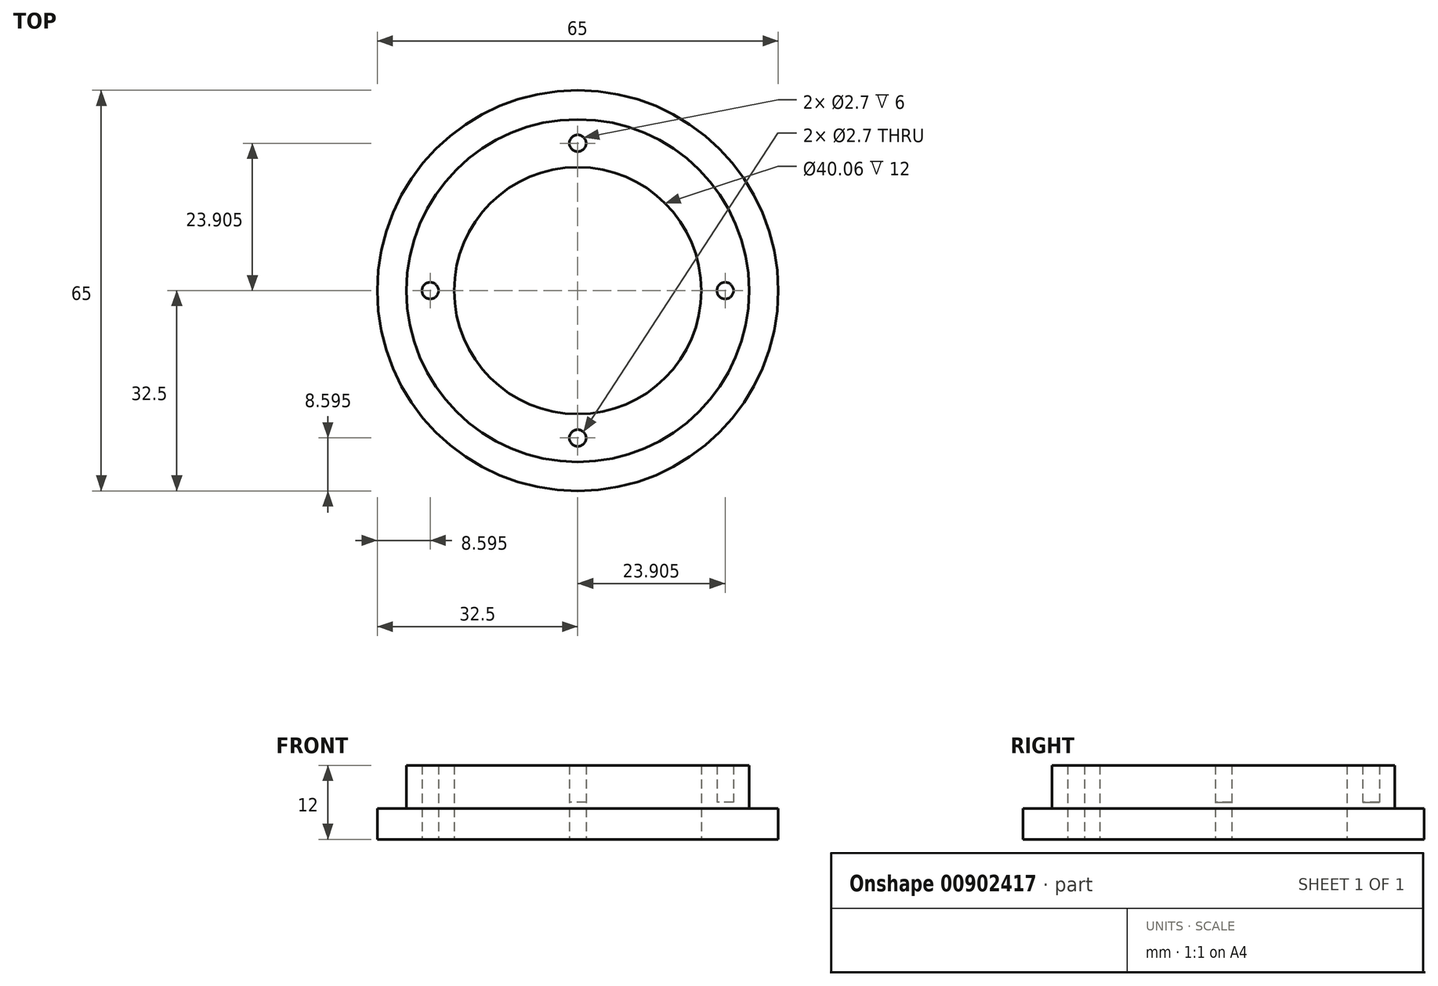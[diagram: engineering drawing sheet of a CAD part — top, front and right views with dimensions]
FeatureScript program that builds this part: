
annotation { "Feature Type Name" : "Feature", "Feature Type Description" : "" }
export const myFeature = defineFeature(function(context is Context, id is Id, definition is map)
    precondition{}
    {
        {
            var Q0;
            Q0=qCreatedBy(makeId("Top.planeOp"),FACE);
            var sketch = newSketch(context, id + "F0", { "sketchPlane" : qUnion([Q0])});
            skCircle(sketch, "E0", {"center": v(0, 0) * mm, "radius": 32.5 * mm});
            skCircle(sketch, "E1.0", {"center": v(0, 0) * mm, "radius": 27.78 * mm});
            skCircle(sketch, "E2.0", {"center": v(0, 0) * mm, "radius": 20.03 * mm});
            skLineSegment(sketch, "E3", {"start": v(0, 56.76) * mm, "end": v(0, -56.47) * mm, "construction": true});
            skLineSegment(sketch, "E4", {"start": v(-75.06, 0) * mm, "end": v(73.64, 0) * mm, "construction": true});
            skCircle(sketch, "E5", {"center": v(0, 23.9) * mm, "radius": 1.35 * mm});
            skCircle(sketch, "E6.MirrorC", {"center": v(0, -23.9) * mm, "radius": 1.35 * mm});
            skCircle(sketch, "E7", {"center": v(23.9, 0) * mm, "radius": 1.35 * mm});
            skCircle(sketch, "E8.MirrorC", {"center": v(-23.9, 0) * mm, "radius": 1.35 * mm});
            skSolve(sketch);
        }
        {
            var Q0;
            Q0=makeQuery(id+"F0.imprint","IMPRINT",FACE,{"disambiguationData":[TD([[makeQuery(id+"F0.imprint","IMPRINT",EDGE,{"derivedFrom":sQuery(id+"F0.wireOp",EDGE,"E0")}),1.0]])]});
            extrude(context, id + "F1", {"entities" : qUnion([Q0]), "depth" : 5 * mm, "offsetDistance" : 25 * mm});
        }
        {
            var Q0;
            Q0=makeQuery(id+"F0.imprint","IMPRINT",FACE,{"disambiguationData":[TD([[makeQuery(id+"F0.imprint","IMPRINT",EDGE,{"derivedFrom":sQuery(id+"F0.wireOp",EDGE,"E1.0")}),1.0]])]});
            extrude(context, id + "F2", {"entities" : qUnion([Q0]), "operationType" : NewBodyOperationType.ADD, "depth" : 12 * mm, "offsetDistance" : 25 * mm});
        }
        {
            var Q0;
            Q0=makeQuery(id+"F0.imprint","IMPRINT",FACE,{"disambiguationData":[TD([[makeQuery(id+"F0.imprint","IMPRINT",EDGE,{"derivedFrom":sQuery(id+"F0.wireOp",EDGE,"E8.MirrorC")}),-1.0]])]});
            var Q1;
            Q1=makeQuery(id+"F0.imprint","IMPRINT",FACE,{"disambiguationData":[TD([[makeQuery(id+"F0.imprint","IMPRINT",EDGE,{"derivedFrom":sQuery(id+"F0.wireOp",EDGE,"E5")}),1.0]])]});
            var Q2;
            Q2=makeQuery(id+"F0.imprint","IMPRINT",FACE,{"disambiguationData":[TD([[makeQuery(id+"F0.imprint","IMPRINT",EDGE,{"derivedFrom":sQuery(id+"F0.wireOp",EDGE,"E7")}),1.0]])]});
            var Q3;
            Q3=makeQuery(id+"F0.imprint","IMPRINT",FACE,{"disambiguationData":[TD([[makeQuery(id+"F0.imprint","IMPRINT",EDGE,{"derivedFrom":sQuery(id+"F0.wireOp",EDGE,"E6.MirrorC")}),-1.0]])]});
            extrude(context, id + "F3", {"entities" : qUnion([Q0, Q1, Q2, Q3]), "operationType" : NewBodyOperationType.ADD, "depth" : 6 * mm, "offsetDistance" : 25 * mm});
        }
    });
